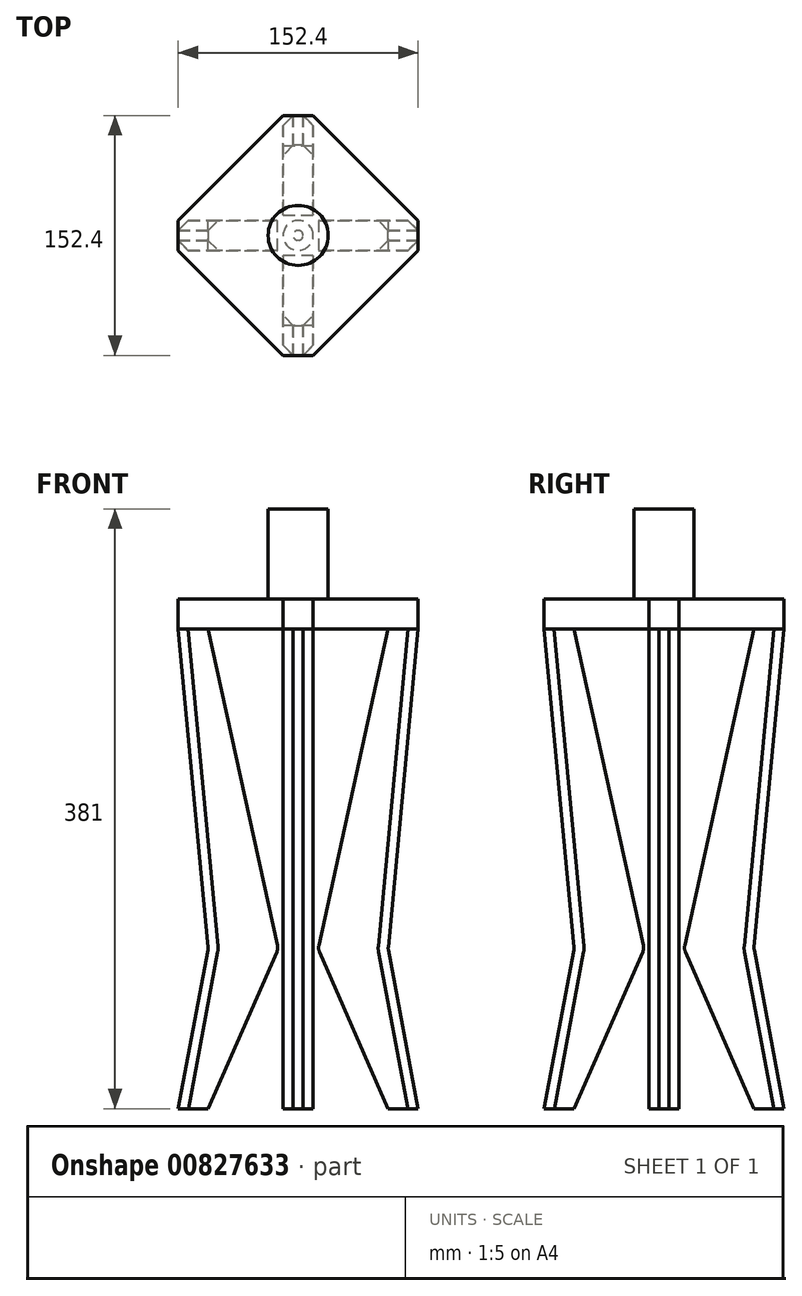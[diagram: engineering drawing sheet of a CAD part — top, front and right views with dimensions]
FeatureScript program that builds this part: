
annotation { "Feature Type Name" : "Feature", "Feature Type Description" : "" }
export const myFeature = defineFeature(function(context is Context, id is Id, definition is map)
    precondition{}
    {
        {
            var Q0;
            Q0=qCreatedBy(makeId("Front.planeOp"),FACE);
            var sketch = newSketch(context, id + "F0", { "sketchPlane" : qUnion([Q0])});
            skLineSegment(sketch, "E0.bottom", {"start": v(-76.2, 304.8) * mm, "end": v(76.2, 304.8) * mm});
            skLineSegment(sketch, "E0.top", {"start": v(-76.2, 0) * mm, "end": v(76.2, 0) * mm});
            skLineSegment(sketch, "E0.left", {"start": v(-76.2, 304.8) * mm, "end": v(-76.2, 0) * mm});
            skLineSegment(sketch, "E0.right", {"start": v(76.2, 304.8) * mm, "end": v(76.2, 0) * mm});
            skLineSegment(sketch, "E1", {"start": v(0, 304.8) * mm, "end": v(0, 0) * mm, "construction": true});
            skLineSegment(sketch, "E2.bottom", {"start": v(-9.53, 323.85) * mm, "end": v(9.52, 323.85) * mm});
            skLineSegment(sketch, "E2.top", {"start": v(-9.53, 304.8) * mm, "end": v(9.52, 304.8) * mm});
            skLineSegment(sketch, "E2.left", {"start": v(-9.53, 323.85) * mm, "end": v(-9.53, 304.8) * mm});
            skLineSegment(sketch, "E2.right", {"start": v(9.52, 323.85) * mm, "end": v(9.52, 304.8) * mm});
            skLineSegment(sketch, "E3.bottom", {"start": v(-19.05, 381) * mm, "end": v(19.05, 381) * mm});
            skLineSegment(sketch, "E3.top", {"start": v(-19.05, 323.85) * mm, "end": v(19.05, 323.85) * mm});
            skLineSegment(sketch, "E3.left", {"start": v(-19.05, 381) * mm, "end": v(-19.05, 323.85) * mm});
            skLineSegment(sketch, "E3.right", {"start": v(19.05, 381) * mm, "end": v(19.05, 323.85) * mm});
            skLineSegment(sketch, "E4", {"start": v(0, 323.85) * mm, "end": v(0, 304.8) * mm});
            skLineSegment(sketch, "E5", {"start": v(-31.75, 304.8) * mm, "end": v(-31.75, 381) * mm});
            skArc(sketch, "E6", {"start": v(-25.4, 508) * mm, "mid": v(-50.67, 445.6) * mm, "end": v(-31.75, 381) * mm});
            skLineSegment(sketch, "E7", {"start": v(-25.4, 508) * mm, "end": v(25.4, 508) * mm});
            skLineSegment(sketch, "E8", {"start": v(0, 508) * mm, "end": v(0, 381) * mm, "construction": true});
            skArc(sketch, "E9.MirrorCS", {"start": v(25.4, 508) * mm, "mid": v(50.67, 445.6) * mm, "end": v(31.75, 381) * mm});
            skLineSegment(sketch, "E10.MirrorCS", {"start": v(31.75, 304.8) * mm, "end": v(31.75, 381) * mm});
            skLineSegment(sketch, "E11", {"start": v(0, 508) * mm, "end": v(-76.2, 508) * mm});
            skLineSegment(sketch, "E12", {"start": v(-76.2, 508) * mm, "end": v(-127, 279.4) * mm});
            skLineSegment(sketch, "E13", {"start": v(-127, 279.4) * mm, "end": v(0, 279.4) * mm});
            skLineSegment(sketch, "E14", {"start": v(-4.76, 304.8) * mm, "end": v(-4.76, 0) * mm});
            skLineSegment(sketch, "E15", {"start": v(0, 381) * mm, "end": v(0, 323.85) * mm});
            skSolve(sketch);
        }
        {
            var Q0;
            Q0=qCreatedBy(makeId("Front.planeOp"),FACE);
            var sketch = newSketch(context, id + "F1", { "sketchPlane" : qUnion([Q0])});
            skLineSegment(sketch, "E16", {"start": v(-76.2, 0) * mm, "end": v(-57.15, 101.6) * mm});
            skLineSegment(sketch, "E17", {"start": v(-57.15, 101.6) * mm, "end": v(-76.2, 304.8) * mm});
            skLineSegment(sketch, "E18", {"start": v(-76.2, 304.8) * mm, "end": v(-57.15, 304.8) * mm});
            skLineSegment(sketch, "E19", {"start": v(-57.15, 304.8) * mm, "end": v(-12.7, 101.6) * mm});
            skLineSegment(sketch, "E20", {"start": v(-12.7, 101.6) * mm, "end": v(-57.15, 0) * mm});
            skLineSegment(sketch, "E21", {"start": v(-76.2, 0) * mm, "end": v(-57.15, 0) * mm});
            skLineSegment(sketch, "E22", {"start": v(-57.15, 101.6) * mm, "end": v(-12.7, 101.6) * mm, "construction": true});
            skSolve(sketch);
        }
        {
            var Q0;
            Q0 = qSketchRegion(id + "F1", true);
            extrude(context, id + "F2", {"entities" : qUnion([Q0]), "endBound" : BoundingType.SYMMETRIC, "depth" : 19.05 * mm, "offsetDistance" : 25.4 * mm});
        }
        {
            var Q0;
            Q0=makeQuery(id+"F2.opExtrude","SWEPT_EDGE",EDGE,{"disambiguationData":[OSD([sQuery(id+"F1.wireOp",EDGE,"E16"),sQuery(id+"F1.wireOp",EDGE,"E17")])]});
            var Q1;
            Q1=makeQuery(id+"F2.opExtrude","SWEPT_EDGE",EDGE,{"disambiguationData":[OSD([sQuery(id+"F1.wireOp",EDGE,"E19"),sQuery(id+"F1.wireOp",EDGE,"E20")])]});
            fillet(context, id + "F3", {"entities" : qUnion([Q0, Q1]), "radius" : 6.35 * mm, "tangentPropagation" : true, "allowEdgeOverflow" : false});
        }
        {
            var Q0;
            Q0=qCreatedBy(makeId("Top.planeOp"),FACE);
            var sketch = newSketch(context, id + "F4", { "sketchPlane" : qUnion([Q0])});
            skCircle(sketch, "E23", {"center": v(0, 0) * mm, "radius": 3.18 * mm});
            skSolve(sketch);
        }
        {
            var Q0;
            Q0 = qSketchRegion(id + "F4", true);
            var Q1;
            Q1=makeQuery(id+"F2.opExtrude","SWEPT_FACE",FACE,{"disambiguationData":[OSD([sQuery(id+"F1.wireOp",EDGE,"E18")])]});
            extrude(context, id + "F5", {"entities" : qUnion([Q0]), "endBound" : BoundingType.UP_TO_SURFACE, "depth" : 25.4 * mm, "endBoundEntityFace" : qUnion([Q1]), "offsetDistance" : 25.4 * mm});
        }
        {
            var Q0;
            {var subQ0=sQuery(id+"F0.wireOp",EDGE,"E3.left");Q0=makeQuery(id+"F0.imprint","IMPRINT",FACE,{"disambiguationData":[TD([[makeQuery(id+"F0.imprint","IMPRINT",EDGE,{"derivedFrom":subQ0}),1.0]])]});}
            var Q1;
            {var subQ1=sQuery(id+"F0.wireOp",EDGE,"E2.left");Q1=makeQuery(id+"F0.imprint","IMPRINT",FACE,{"disambiguationData":[TD([[makeQuery(id+"F0.imprint","IMPRINT",EDGE,{"derivedFrom":subQ1}),1.0]])]});}
            var Q2;
            Q2=sQuery(id+"F0.wireOp",EDGE,"E15");
            revolve(context, id + "F6", {"operationType" : NewBodyOperationType.ADD, "surfaceOperationType" : NewSurfaceOperationType.NEW, "entities" : qUnion([Q0, Q1]), "axis" : qUnion([Q2]), "revolveType" : RevolveType.FULL});
        }
        {
            var Q0;
            Q0=sQuery(id+"F0.wireOp",EDGE,"E12");
            extrude(context, id + "F7", {"bodyType" : ToolBodyType.SURFACE, "surfaceEntities" : qUnion([Q0]), "endBound" : BoundingType.SYMMETRIC, "depth" : 254 * mm, "offsetDistance" : 25.4 * mm});
        }
        {
            var Q0;
            Q0=makeQuery(id+"F2.opExtrude","CAP_EDGE",EDGE,{"disambiguationData":[OSD([sQuery(id+"F1.wireOp",EDGE,"E17")])],"isStart":false});
            var Q1;
            Q1=makeQuery(id+"F2.opExtrude","CAP_EDGE",EDGE,{"disambiguationData":[OSD([sQuery(id+"F1.wireOp",EDGE,"E17")])],"isStart":true});
            chamfer(context, id + "F8", {"entities" : qUnion([Q0, Q1]), "width" : 6.35 * mm, "tangentPropagation" : true});
        }
        {
            var Q0;
            Q0=makeQuery(id+"F7.opExtrude","SWEPT_BODY",BODY,{"disambiguationData":[OSD([sQuery(id+"F0.wireOp",EDGE,"E12")])]});
            var Q1;
            Q1=sQuery(id+"F0.wireOp",EDGE,"E8");
            circularPattern(context, id + "F9", {"entities" : qUnion([Q0]), "axis" : qUnion([Q1]), "angle" : 360 * degree, "instanceCount" : 4, "equalSpace" : true});
        }
        {
            var Q0;
            Q0=makeQuery(id+"F2.opExtrude","SWEPT_BODY",BODY,{"disambiguationData":[OSD([sQuery(id+"F1.wireOp",EDGE,"E16"),sQuery(id+"F1.wireOp",EDGE,"E17"),sQuery(id+"F1.wireOp",EDGE,"E18"),sQuery(id+"F1.wireOp",EDGE,"E19"),sQuery(id+"F1.wireOp",EDGE,"E20"),sQuery(id+"F1.wireOp",EDGE,"E21")])]});
            var Q1;
            Q1=sQuery(id+"F0.wireOp",EDGE,"E1");
            circularPattern(context, id + "F10", {"entities" : qUnion([Q0]), "axis" : qUnion([Q1]), "angle" : 360 * degree, "instanceCount" : 4, "equalSpace" : true});
        }
        {
            var Q0;
            Q0=makeQuery(id+"F10.opPattern","COPY",FACE,{"derivedFrom":makeQuery(id+"F2.opExtrude","SWEPT_FACE",FACE,{"disambiguationData":[OSD([sQuery(id+"F1.wireOp",EDGE,"E18")])]}),"instanceName":"3"});
            var sketch = newSketch(context, id + "F11", { "sketchPlane" : qUnion([Q0])});
            skLineSegment(sketch, "E24.0", {"start": v(-9.53, 76.2) * mm, "end": v(9.52, 76.2) * mm});
            skLineSegment(sketch, "E24.1", {"start": v(-76.2, -9.53) * mm, "end": v(-76.2, 9.52) * mm});
            skLineSegment(sketch, "E24.2", {"start": v(9.52, -76.2) * mm, "end": v(-9.53, -76.2) * mm});
            skLineSegment(sketch, "E24.3", {"start": v(76.2, 9.53) * mm, "end": v(76.2, -9.52) * mm});
            skLineSegment(sketch, "E25", {"start": v(9.52, 76.2) * mm, "end": v(76.2, 9.53) * mm});
            skLineSegment(sketch, "E26", {"start": v(76.2, -9.52) * mm, "end": v(9.52, -76.2) * mm});
            skLineSegment(sketch, "E27", {"start": v(-9.52, -76.2) * mm, "end": v(-76.2, -9.52) * mm});
            skLineSegment(sketch, "E28", {"start": v(-76.2, 9.52) * mm, "end": v(-9.53, 76.2) * mm});
            skSolve(sketch);
        }
        {
            var Q0;
            Q0 = qSketchRegion(id + "F11", true);
            extrude(context, id + "F12", {"entities" : qUnion([Q0]), "depth" : 19.05 * mm, "offsetDistance" : 25.4 * mm});
        }
    });
